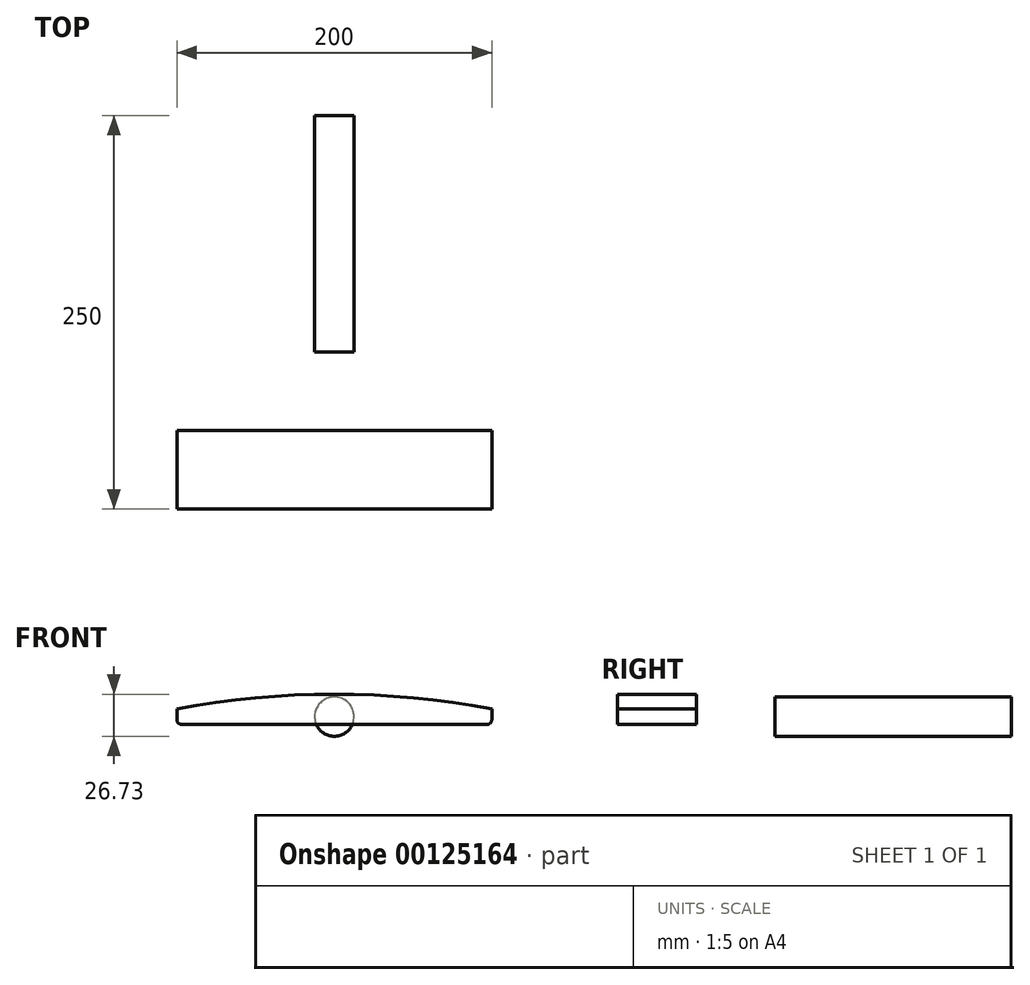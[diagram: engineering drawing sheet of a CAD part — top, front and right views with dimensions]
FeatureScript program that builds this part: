
annotation { "Feature Type Name" : "Feature", "Feature Type Description" : "" }
export const myFeature = defineFeature(function(context is Context, id is Id, definition is map)
    precondition{}
    {
        {
            var Q0;
            Q0=qCreatedBy(makeId("Front.planeOp"),FACE);
            var sketch = newSketch(context, id + "F0", { "sketchPlane" : qUnion([Q0])});
            skArc(sketch, "E0", {"start": v(-3.37, 12.04) * mm, "mid": v(-11.58, 4.72) * mm, "end": v(-10.83, -6.25) * mm});
            skArc(sketch, "E1", {"start": v(3.37, 12.04) * mm, "mid": v(0, 12.5) * mm, "end": v(-3.37, 12.04) * mm});
            skArc(sketch, "E2", {"start": v(10.83, -6.25) * mm, "mid": v(11.58, 4.72) * mm, "end": v(3.37, 12.04) * mm});
            skArc(sketch, "E3", {"start": v(-10.83, -6.25) * mm, "mid": v(0, -12.5) * mm, "end": v(10.83, -6.25) * mm});
            skPoint(sketch, "E4.MirrorCS.end.orphan", {"position": v(-3.37, 12.04) * mm});
            skLineSegment(sketch, "E5", {"start": v(0, 0) * mm, "end": v(-3.37, 12.04) * mm});
            skLineSegment(sketch, "E6", {"start": v(0, 0) * mm, "end": v(3.37, 12.04) * mm});
            skLineSegment(sketch, "E7", {"start": v(0, 0) * mm, "end": v(10.83, -6.25) * mm});
            skLineSegment(sketch, "E8", {"start": v(0, 0) * mm, "end": v(-10.83, -6.25) * mm});
            skSolve(sketch);
        }
        {
            var Q0;
            Q0=qCreatedBy(makeId("Front.planeOp"),FACE);
            var sketch = newSketch(context, id + "F1", { "sketchPlane" : qUnion([Q0])});
            skLineSegment(sketch, "E9.bottom", {"start": v(100, 5) * mm, "end": v(-100, 5) * mm});
            skLineSegment(sketch, "E9.top", {"start": v(97, -5) * mm, "end": v(-97, -5) * mm});
            skLineSegment(sketch, "E9.left", {"start": v(100, 5) * mm, "end": v(100, -2) * mm});
            skLineSegment(sketch, "E9.right", {"start": v(-100, 5) * mm, "end": v(-100, -2) * mm});
            skPoint(sketch, "E9.middle", {"position": v(0, 0) * mm});
            skPoint(sketch, "E10.visualSharp", {"position": v(100, -5) * mm});
            skArc(sketch, "E10.filletArc", {"start": v(97, -5) * mm, "mid": v(99.12, -4.12) * mm, "end": v(100, -2) * mm});
            skArc(sketch, "E11", {"start": v(100, 5) * mm, "mid": v(0, 14.23) * mm, "end": v(-100, 5) * mm});
            skPoint(sketch, "E12.visualSharp", {"position": v(-100, -5) * mm});
            skArc(sketch, "E12.filletArc", {"start": v(-100, -2) * mm, "mid": v(-99.12, -4.12) * mm, "end": v(-97, -5) * mm});
            skSolve(sketch);
        }
        {
            var Q0;
            Q0 = qSketchRegion(id + "F1", true);
            extrude(context, id + "F2", {"entities" : qUnion([Q0]), "depth" : 50 * mm});
        }
        {
            var Q0;
            Q0=makeQuery(id+"F0.imprint","IMPRINT",FACE,{"disambiguationData":[TD([[makeQuery(id+"F0.imprint","IMPRINT",EDGE,{"derivedFrom":sQuery(id+"F0.wireOp",EDGE,"E0")}),1.0]])]});
            var Q1;
            Q1=makeQuery(id+"F0.imprint","IMPRINT",FACE,{"disambiguationData":[TD([[makeQuery(id+"F0.imprint","IMPRINT",EDGE,{"derivedFrom":sQuery(id+"F0.wireOp",EDGE,"E1")}),1.0]])]});
            var Q2;
            Q2=makeQuery(id+"F0.imprint","IMPRINT",FACE,{"disambiguationData":[TD([[makeQuery(id+"F0.imprint","IMPRINT",EDGE,{"derivedFrom":sQuery(id+"F0.wireOp",EDGE,"E2")}),1.0]])]});
            var Q3;
            Q3=makeQuery(id+"F0.imprint","IMPRINT",FACE,{"disambiguationData":[TD([[makeQuery(id+"F0.imprint","IMPRINT",EDGE,{"derivedFrom":sQuery(id+"F0.wireOp",EDGE,"E3")}),1.0]])]});
            extrude(context, id + "F3", {"entities" : qUnion([Q0, Q1, Q2, Q3]), "oppositeDirection" : true, "depth" : 150 * mm});
        }
        {
            var Q0;
            Q0=makeQuery(id+"F2.opExtrude","SWEPT_BODY",BODY,{"disambiguationData":[OSD([sQuery(id+"F1.wireOp",EDGE,"E9.top"),sQuery(id+"F1.wireOp",EDGE,"E9.left"),sQuery(id+"F1.wireOp",EDGE,"E9.right"),sQuery(id+"F1.wireOp",EDGE,"E10.filletArc"),sQuery(id+"F1.wireOp",EDGE,"E11"),sQuery(id+"F1.wireOp",EDGE,"E12.filletArc")])]});
            transform(context, id + "F4", {"entities" : qUnion([Q0]), "transformType" : TransformType.TRANSLATION_3D, "dx" : 0 * mm, "dy" : -50 * mm, "dz" : 0 * mm, "makeCopy" : false});
        }
        {
            var Q0;
            Q0=makeQuery(id+"F2.opExtrude","CAP_FACE",FACE,{"disambiguationData":[OSD([sQuery(id+"F1.wireOp",EDGE,"E9.top"),sQuery(id+"F1.wireOp",EDGE,"E9.left"),sQuery(id+"F1.wireOp",EDGE,"E9.right"),sQuery(id+"F1.wireOp",EDGE,"E10.filletArc"),sQuery(id+"F1.wireOp",EDGE,"E11"),sQuery(id+"F1.wireOp",EDGE,"E12.filletArc")])],"isStart":true});
            var sketch = newSketch(context, id + "F5", { "sketchPlane" : qUnion([Q0])});
            skLineSegment(sketch, "E13", {"start": v(0, -5) * mm, "end": v(0, 14.23) * mm, "construction": true});
            skLineSegment(sketch, "E14", {"start": v(-23.3, -5) * mm, "end": v(-23.3, 13.73) * mm});
            skLineSegment(sketch, "E15.MirrorCS", {"start": v(23.3, -5) * mm, "end": v(23.3, 13.73) * mm});
            skArc(sketch, "E16.0", {"start": v(-23.3, 13.73) * mm, "mid": v(0, 14.23) * mm, "end": v(23.3, 13.73) * mm});
            skLineSegment(sketch, "E17.0", {"start": v(-23.3, -5) * mm, "end": v(23.3, -5) * mm});
            skPoint(sketch, "E18.orphan", {"position": v(-100, 5) * mm});
            skPoint(sketch, "E19.orphan", {"position": v(100, 5) * mm});
            skPoint(sketch, "E20.orphan", {"position": v(97, -5) * mm});
            skPoint(sketch, "E21.orphan", {"position": v(-97, -5) * mm});
            skSolve(sketch);
        }
        {
            var Q0;
            Q0=sQuery(id+"F0.wireOp",VERTEX,"E6.end");
            var Q1;
            Q1=sQuery(id+"F5.wireOp",VERTEX,"E16.0.start");
            var Q2;
            Q2=sQuery(id+"F5.wireOp",VERTEX,"E17.0.start");
            cPlane(context, id + "F6", {"entities" : qUnion([Q0, Q1, Q2]), "cplaneType" : CPlaneType.THREE_POINT, "offset" : 25 * mm, "width" : 150 * mm, "height" : 150 * mm});
        }
    });
